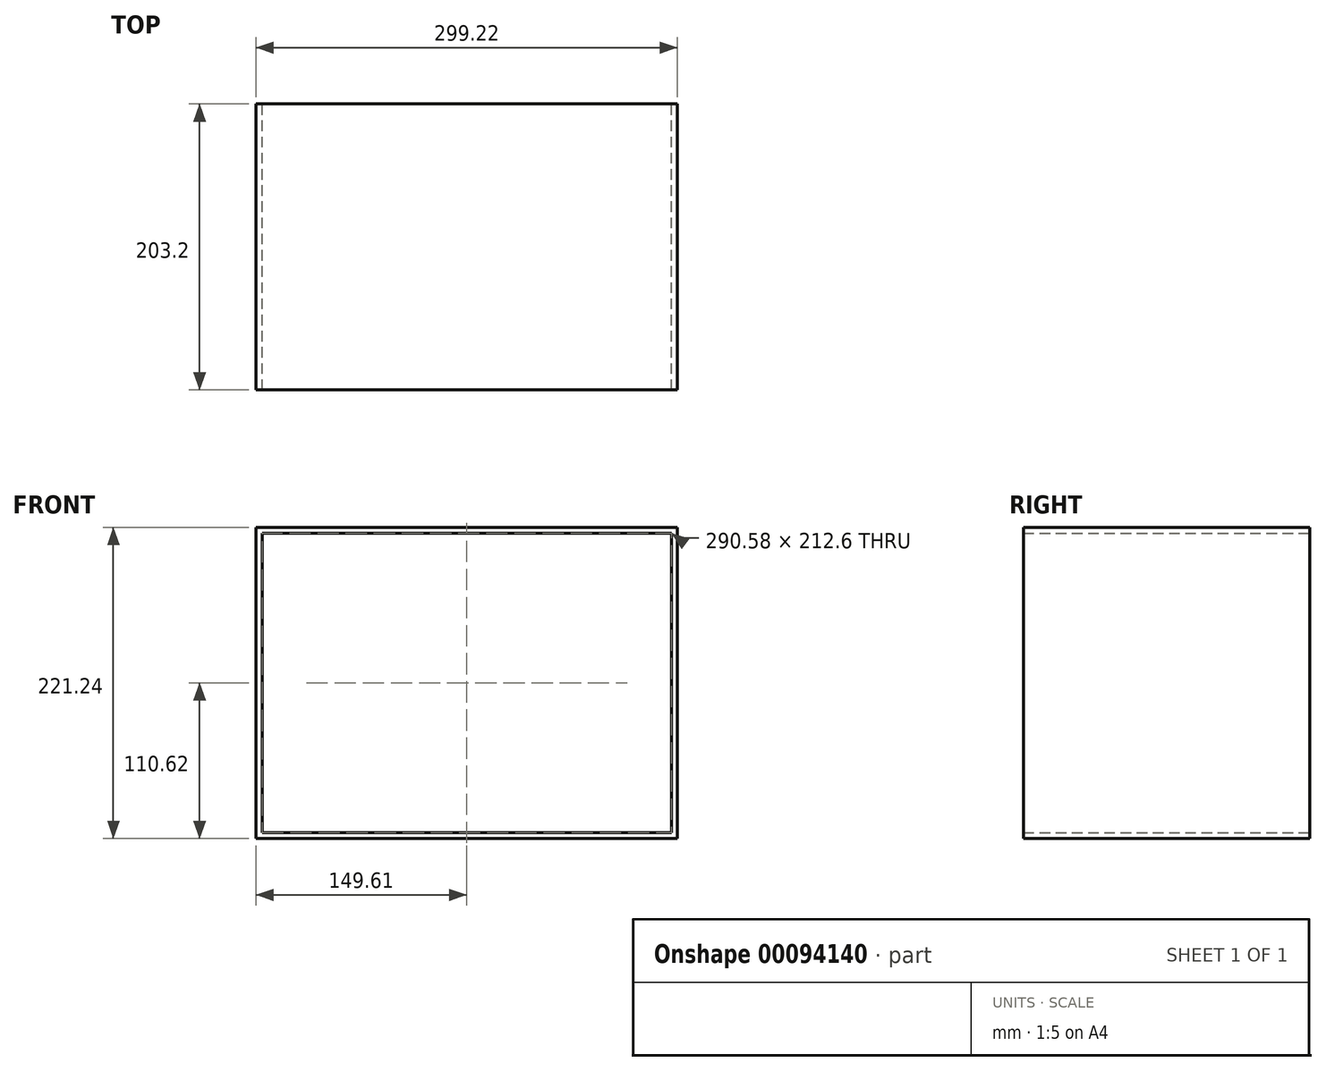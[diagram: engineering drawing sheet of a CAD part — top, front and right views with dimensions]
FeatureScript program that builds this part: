
annotation { "Feature Type Name" : "Feature", "Feature Type Description" : "" }
export const myFeature = defineFeature(function(context is Context, id is Id, definition is map)
    precondition{}
    {
        {
            var Q0;
            Q0=qCreatedBy(makeId("Front.planeOp"),FACE);
            var sketch = newSketch(context, id + "F0", { "sketchPlane" : qUnion([Q0])});
            skLineSegment(sketch, "E0.bottom", {"start": v(145.29, 106.3) * mm, "end": v(-145.29, 106.3) * mm});
            skLineSegment(sketch, "E0.top", {"start": v(145.29, -106.3) * mm, "end": v(-145.29, -106.3) * mm});
            skLineSegment(sketch, "E0.left", {"start": v(145.29, 106.3) * mm, "end": v(145.29, -106.3) * mm});
            skLineSegment(sketch, "E0.right", {"start": v(-145.29, 106.3) * mm, "end": v(-145.29, -106.3) * mm});
            skPoint(sketch, "E0.middle", {"position": v(0, 0) * mm});
            skPoint(sketch, "E1.bottom.end.orphan", {"position": v(-143.13, 104.14) * mm});
            skPoint(sketch, "E1.left.start.orphan", {"position": v(143.13, 104.14) * mm});
            skPoint(sketch, "E1.top.end.orphan", {"position": v(-143.13, -104.14) * mm});
            skPoint(sketch, "E1.top.start.orphan", {"position": v(143.13, -104.14) * mm});
            skLineSegment(sketch, "E2.bottom", {"start": v(-149.6, -110.62) * mm, "end": v(149.6, -110.62) * mm});
            skLineSegment(sketch, "E2.top", {"start": v(-149.6, 110.62) * mm, "end": v(149.6, 110.62) * mm});
            skLineSegment(sketch, "E2.left", {"start": v(-149.6, -110.62) * mm, "end": v(-149.6, 110.62) * mm});
            skLineSegment(sketch, "E2.right", {"start": v(149.6, -110.62) * mm, "end": v(149.6, 110.62) * mm});
            skSolve(sketch);
        }
        {
            var Q0;
            Q0=makeQuery(id+"F0.imprint","IMPRINT",FACE,{"disambiguationData":[TD([[makeQuery(id+"F0.imprint","IMPRINT",EDGE,{"derivedFrom":sQuery(id+"F0.wireOp",EDGE,"E0.bottom")}),-1.0]])]});
            extrude(context, id + "F1", {"entities" : qUnion([Q0]), "depth" : 203.2 * mm});
        }
    });
